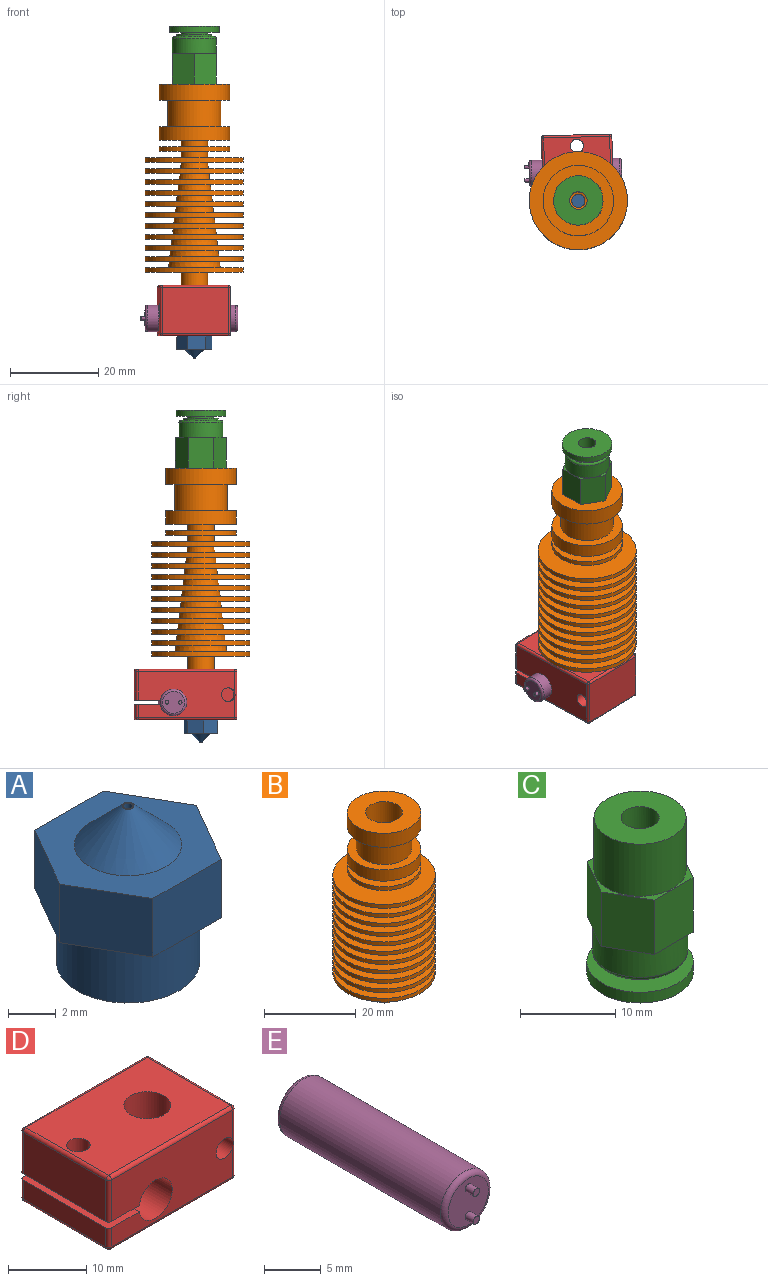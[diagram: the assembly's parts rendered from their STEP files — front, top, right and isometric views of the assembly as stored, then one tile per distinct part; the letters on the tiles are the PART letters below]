
ASSEMBLY  parts=5 mates=7
PART A: 14 faces, bbox 8.1x7x8 mm
  f0: plane 3.5x3mm, normal (0.87,-0.5,0), area 12.1mm2, adj f1,f5,f7,f8
  f1: plane 3.5x3mm, normal (0.87,0.5,0), area 12.1mm2, adj f0,f2,f7,f8
  f2: plane 4.04x3mm, normal (0,1,0), area 12.1mm2, adj f1,f3,f7,f8
  f3: plane 3.5x3mm, normal (-0.87,0.5,0), area 12.1mm2, adj f2,f4,f7,f8
  f4: plane 3.5x3mm, normal (-0.87,-0.5,0), area 12.1mm2, adj f3,f5,f7,f8
  f5: plane 4.04x3mm, normal (0,-1,0), area 12.1mm2, adj f0,f4,f7,f8
  f6: cylinder r=0.2mm len=5mm, axis (0,0,-1), area 6.3mm2, adj f9,f13
  f7: plane 8.08x7mm, normal (0,0,1), area 26.5mm2, adj f0,f1,f2,f3,f4,f5,f10
  f8: plane 8.08x7mm, normal (0,0,-1), area 14.2mm2, adj f0,f1,f2,f3,f4,f5,f12
  f9: plane 0.5x0.5mm, normal (0,0,1), area 0.1mm2, adj f6,f10
  f10: cone r=0.25mm half-angle=45deg, axis (0,0,-1), area 22.2mm2, adj f7,f9
  f11: plane 6x6mm, normal (0,0,-1), area 28.3mm2, adj f12
  f12: cylinder r=3mm len=6mm, axis (0,0,1), area 56.5mm2, adj f8,f11
  f13: plane 0.4x0.4mm, normal (0,0,1), area 0.1mm2, adj f6
PART B: 64 faces, bbox 22.3x22.3x48.7 mm
  f0: plane 22.3x22.3mm, normal (0,0,1), area 282mm2, adj f1,f63
  f1: cone r=5.7mm half-angle=6.8deg, axis (0,0,-1), area 55mm2, adj f0,f2
  f2: plane 22.3x22.3mm, normal (0,0,-1), area 288.5mm2, adj f1,f3
  f3: cylinder r=11.15mm len=22.3mm, axis (0,0,1), area 70.1mm2, adj f2,f4
  f4: plane 22.3x22.3mm, normal (0,0,1), area 292.8mm2, adj f3,f5
  f5: cone r=5.4mm half-angle=6.8deg, axis (0,0,-1), area 52.1mm2, adj f4,f6
  f6: plane 22.3x22.3mm, normal (0,0,-1), area 299mm2, adj f5,f7
  f7: cylinder r=11.15mm len=22.3mm, axis (0,0,1), area 70.1mm2, adj f6,f8
  f8: plane 22.3x22.3mm, normal (0,0,1), area 303mm2, adj f7,f9
  f9: cone r=5.1mm half-angle=6.8deg, axis (0,0,-1), area 49.3mm2, adj f8,f10
  f10: plane 22.3x22.3mm, normal (0,0,-1), area 308.9mm2, adj f9,f11
  f11: cylinder r=11.15mm len=22.3mm, axis (0,0,1), area 70.1mm2, adj f10,f12
  f12: plane 22.3x22.3mm, normal (0,0,1), area 312.7mm2, adj f11,f13
  f13: cone r=4.8mm half-angle=6.8deg, axis (0,0,-1), area 46.4mm2, adj f12,f14
  f14: plane 22.3x22.3mm, normal (0,0,-1), area 318.2mm2, adj f13,f15
  f15: cylinder r=11.15mm len=22.3mm, axis (0,0,1), area 70.1mm2, adj f14,f16
  f16: plane 22.3x22.3mm, normal (0,0,1), area 321.8mm2, adj f15,f17
  f17: cone r=4.5mm half-angle=6.8deg, axis (0,0,-1), area 43.6mm2, adj f16,f18
  f18: plane 22.3x22.3mm, normal (0,0,-1), area 327mm2, adj f17,f19
  f19: cylinder r=11.15mm len=22.3mm, axis (0,0,1), area 70.1mm2, adj f18,f20
  f20: plane 22.3x22.3mm, normal (0,0,1), area 330.3mm2, adj f19,f21
  f21: cone r=4.2mm half-angle=6.8deg, axis (0,0,-1), area 40.7mm2, adj f20,f22
  f22: plane 22.3x22.3mm, normal (0,0,-1), area 335.2mm2, adj f21,f23
  f23: cylinder r=11.15mm len=22.3mm, axis (0,0,1), area 70.1mm2, adj f22,f24
  f24: plane 22.3x22.3mm, normal (0,0,1), area 338.3mm2, adj f23,f25
  f25: cone r=3.9mm half-angle=6.8deg, axis (0,0,-1), area 37.9mm2, adj f24,f26
  f26: plane 22.3x22.3mm, normal (0,0,-1), area 342.8mm2, adj f25,f27
  f27: cylinder r=11.15mm len=22.3mm, axis (0,0,1), area 70.1mm2, adj f26,f28
  f28: plane 22.3x22.3mm, normal (0,0,1), area 345.7mm2, adj f27,f29
  f29: cone r=3.6mm half-angle=6.8deg, axis (0,0,-1), area 35mm2, adj f28,f30
  f30: plane 22.3x22.3mm, normal (0,0,-1), area 349.9mm2, adj f29,f31
  f31: cylinder r=11.15mm len=22.3mm, axis (0,0,1), area 70.1mm2, adj f30,f32
  f32: plane 22.3x22.3mm, normal (0,0,1), area 352.5mm2, adj f31,f33
  f33: cone r=3.3mm half-angle=6.8deg, axis (0,0,-1), area 32.2mm2, adj f32,f34
  f34: plane 22.3x22.3mm, normal (0,0,-1), area 356.4mm2, adj f33,f35
  f35: cylinder r=11.15mm len=22.3mm, axis (0,0,1), area 70.1mm2, adj f34,f36
  f36: plane 22.3x22.3mm, normal (0,0,1), area 358.8mm2, adj f35,f37
  f37: cone r=3mm half-angle=6.8deg, axis (0,0,-1), area 29.3mm2, adj f36,f38
  f38: plane 22.3x22.3mm, normal (0,0,-1), area 362.3mm2, adj f37,f39
  f39: cylinder r=11.15mm len=22.3mm, axis (0,0,1), area 70.1mm2, adj f38,f40
  f40: plane 22.3x22.3mm, normal (0,0,1), area 362.3mm2, adj f39,f41
  f41: cylinder r=3mm len=6mm, axis (0,0,1), area 28.3mm2, adj f40,f42
  f42: plane 16x16mm, normal (0,0,-1), area 172.8mm2, adj f41,f43
  f43: cylinder r=8mm len=16mm, axis (0,0,1), area 50.3mm2, adj f42,f44
  f44: plane 16x16mm, normal (0,0,1), area 172.8mm2, adj f43,f45
  f45: cylinder r=3mm len=6mm, axis (0,0,1), area 28.3mm2, adj f44,f46
  f46: plane 16x16mm, normal (0,0,-1), area 172.8mm2, adj f45,f47
  f47: cylinder r=8mm len=16mm, axis (0,0,1), area 150.8mm2, adj f46,f48
  f48: plane 16x16mm, normal (0,0,1), area 88mm2, adj f47,f49
  f49: cylinder r=6mm len=12mm, axis (0,0,1), area 226.2mm2, adj f48,f50
  f50: plane 16x16mm, normal (0,0,-1), area 88mm2, adj f49,f51
  f51: cylinder r=8mm len=16mm, axis (0,0,1), area 186mm2, adj f50,f52
  f52: plane 16x16mm, normal (0,0,1), area 150.8mm2, adj f51,f53
  f53: cylinder r=4mm len=8mm, axis (0,0,1), area 165.7mm2, adj f52,f54
  f54: cone r=4mm half-angle=46.2deg, axis (0,0,1), area 52.2mm2, adj f53,f55
  f55: cylinder r=2mm len=24.95mm, axis (0,0,1), area 313.5mm2, adj f54,f56
  f56: plane 7x7mm, normal (0,0,-1), area 25.9mm2, adj f55,f57
  f57: cylinder r=3.5mm len=8.24mm, axis (0,0,1), area 181.2mm2, adj f56,f58
  f58: cone r=1.5mm half-angle=74.1deg, axis (0,0,1), area 32.7mm2, adj f57,f59
  f59: cylinder r=1.5mm len=6.43mm, axis (0,0,1), area 60.6mm2, adj f58,f60
  f60: plane 6x6mm, normal (0,0,-1), area 21.2mm2, adj f59,f61
  f61: cylinder r=3mm len=6mm, axis (0,0,1), area 113.1mm2, adj f60,f62
  f62: plane 22.3x22.3mm, normal (0,0,-1), area 362.3mm2, adj f61,f63
  f63: cylinder r=11.15mm len=22.3mm, axis (0,0,1), area 70.1mm2, adj f0,f62
PART C: 25 faces, bbox 11.5x11.2x19.9 mm
  f0: cylinder r=5.61mm len=11.22mm, axis (0,0,-1), area 48.3mm2, adj f1,f2
  f1: plane 11.22x11.22mm, normal (0,0,1), area 70.6mm2, adj f0,f3
  f2: plane 11.22x11.22mm, normal (0,0,-1), area 86.3mm2, adj f0,f24
  f3: cylinder r=3mm len=6mm, axis (0,0,-1), area 9.4mm2, adj f1,f5
  f4: cylinder r=4mm len=8mm, axis (0,0,-1), area 12.6mm2, adj f5,f7
  f5: plane 8x8mm, normal (0,0,-1), area 22mm2, adj f3,f4
  f6: cylinder r=5mm len=10mm, axis (0,0,-1), area 105.2mm2, adj f8,f9,f10,f11,f12,f13,f14
  f7: plane 9x9mm, normal (0,0,-1), area 13.4mm2, adj f4,f8
  f8: torus R=4.5mm, axis (0,0,1), area 23.8mm2, adj f6,f7
  f9: plane 4.33x2.5mm, normal (0,0,-1), area 1.3mm2, adj f6,f17,f18
  f10: plane 4.33x2.5mm, normal (0,0,-1), area 1.3mm2, adj f6,f18,f19
  f11: plane 5x1.44mm, normal (0,0,-1), area 1.3mm2, adj f6,f19,f20
  f12: plane 4.33x2.5mm, normal (0,0,-1), area 1.3mm2, adj f6,f15,f20
  f13: plane 4.33x2.5mm, normal (0,0,-1), area 1.3mm2, adj f6,f15,f16
  f14: plane 5x1.44mm, normal (0,0,-1), area 1.3mm2, adj f6,f16,f17
  f15: plane 7x5.77mm, normal (0,-1,0), area 40.4mm2, adj f12,f13,f16,f20,f21
  f16: plane 7x5mm, normal (0.87,-0.5,0), area 40.4mm2, adj f13,f14,f15,f17,f21
  f17: plane 7x5mm, normal (0.87,0.5,0), area 40.4mm2, adj f9,f14,f16,f18,f21
  f18: plane 7x5.77mm, normal (0,1,0), area 40.4mm2, adj f9,f10,f17,f19,f21
  f19: plane 7x5mm, normal (-0.87,0.5,0), area 40.4mm2, adj f10,f11,f18,f20,f21
  f20: plane 7x5mm, normal (-0.87,-0.5,0), area 40.4mm2, adj f11,f12,f15,f19,f21
  f21: plane 11.55x10mm, normal (0,0,1), area 12.7mm2, adj f15,f16,f17,f18,f19,f20,f22
  f22: cylinder r=4.85mm len=9.7mm, axis (0,0,-1), area 204.2mm2, adj f21,f23
  f23: plane 9.7x9.7mm, normal (0,0,1), area 61.3mm2, adj f22,f24
  f24: cylinder r=2mm len=19.92mm, axis (0,0,-1), area 250.3mm2, adj f2,f23
PART D: 37 faces, bbox 23x16x11.5 mm
  f0: plane 22x15mm, normal (0,0,-1), area 294.7mm2, adj f12,f14,f25,f30,f33,f36
  f1: plane 15x10.5mm, normal (1,0,0), area 157.5mm2, adj f22,f31,f32,f36
  f2: plane 22x15mm, normal (0,0,1), area 294.7mm2, adj f13,f14,f16,f21,f22,f23
  f3: plane 15x6.5mm, normal (-1,0,0), area 97.5mm2, adj f4,f15,f16,f17
  f4: plane 16x5.54mm, normal (0,0,-1), area 81.5mm2, adj f3,f5,f8,f9,f13,f15,f17
  f5: cylinder r=3mm len=16mm, axis (0,1,0), area 285.5mm2, adj f4,f6,f8,f9
  f6: plane 16x5.54mm, normal (0,0,1), area 81.5mm2, adj f5,f7,f8,f9,f12,f20,f24
  f7: plane 15x3mm, normal (-1,0,0), area 45mm2, adj f6,f20,f24,f25
  f8: plane 22x10.5mm, normal (0,-1,0), area 190.2mm2, adj f4,f5,f6,f10,f15,f20,f21,f30
  f9: plane 22x10.5mm, normal (0,1,0), area 197.7mm2, adj f4,f5,f6,f17,f23,f24,f32,f33
  f10: cylinder r=1.55mm len=10mm, axis (0,-1,0), area 97.4mm2, adj f8,f11,f31
  f11: plane 3.1x3.1mm, normal (0,-1,0), area 7.5mm2, adj f10
  f12: cylinder r=1.5mm len=3.5mm, axis (0,0,1), area 33mm2, adj f0,f6
  f13: cylinder r=1.5mm len=7mm, axis (0,0,1), area 66mm2, adj f2,f4
  f14: cylinder r=3mm len=11.5mm, axis (0,0,1), area 216.8mm2, adj f0,f2
  f15: cylinder r=0.5mm len=6.5mm, axis (0,0,1), area 5.1mm2, adj f3,f4,f8,f18
  f16: cylinder r=0.5mm len=15mm, axis (0,-1,0), area 11.8mm2, adj f2,f3,f18,f19
  f17: cylinder r=0.5mm len=6.5mm, axis (0,0,-1), area 5.1mm2, adj f3,f4,f9,f19
  f18: sphere r=0.5mm, area 0.4mm2, adj f15,f16,f21
  f19: sphere r=0.5mm, area 0.4mm2, adj f16,f17,f23
  f20: cylinder r=0.5mm len=3mm, axis (0,0,1), area 2.4mm2, adj f6,f7,f8,f26
  f21: cylinder r=0.5mm len=22mm, axis (1,0,0), area 17.3mm2, adj f2,f8,f18,f27
  f22: cylinder r=0.5mm len=15mm, axis (0,1,0), area 11.8mm2, adj f1,f2,f27,f28
  f23: cylinder r=0.5mm len=22mm, axis (-1,0,0), area 17.3mm2, adj f2,f9,f19,f28
  f24: cylinder r=0.5mm len=3mm, axis (0,0,-1), area 2.4mm2, adj f6,f7,f9,f29
  f25: cylinder r=0.5mm len=15mm, axis (0,1,0), area 11.8mm2, adj f0,f7,f26,f29
  f26: sphere r=0.5mm, area 0.4mm2, adj f20,f25,f30
  f27: sphere r=0.5mm, area 0.4mm2, adj f21,f22,f31
  f28: sphere r=0.5mm, area 0.4mm2, adj f22,f23,f32
  f29: sphere r=0.5mm, area 0.4mm2, adj f24,f25,f33
  f30: cylinder r=0.5mm len=22mm, axis (-1,0,0), area 17.3mm2, adj f0,f8,f26,f34
  f31: cylinder r=0.5mm len=10.5mm, axis (0,0,-1), area 8.2mm2, adj f1,f8,f10,f27,f34
  f32: cylinder r=0.5mm len=10.5mm, axis (0,0,1), area 8.2mm2, adj f1,f9,f28,f35
  f33: cylinder r=0.5mm len=22mm, axis (1,0,0), area 17.3mm2, adj f0,f9,f29,f35
  f34: sphere r=0.5mm, area 0.4mm2, adj f30,f31,f36
  f35: sphere r=0.5mm, area 0.4mm2, adj f32,f33,f36
  f36: cylinder r=0.5mm len=15mm, axis (0,-1,0), area 11.8mm2, adj f0,f1,f34,f35
PART E: 9 faces, bbox 6.5x22x6.5 mm
  f0: cylinder r=3mm len=20mm, axis (0,1,0), area 377mm2, adj f3,f4
  f1: plane 5x5mm, normal (0,-1,0), area 18.6mm2, adj f4,f5,f7
  f2: plane 5x5mm, normal (0,1,0), area 19.6mm2, adj f3
  f3: torus R=2.5mm, axis (0,-1,0), area 13.9mm2, adj f0,f2
  f4: torus R=2.5mm, axis (0,-1,0), area 13.9mm2, adj f0,f1
  f5: cylinder r=0.4mm len=1mm, axis (0,1,0), area 2.5mm2, adj f1,f6
  f6: plane 0.8x0.8mm, normal (0,-1,0), area 0.5mm2, adj f5
  f7: cylinder r=0.4mm len=1mm, axis (0,1,0), area 2.5mm2, adj f1,f8
  f8: plane 0.8x0.8mm, normal (0,-1,0), area 0.5mm2, adj f7
PLACE A rot(axis=(0.43,0.9,0),180deg) t=(-6.41,22.84,-22.76)mm
PLACE B t=(-6.41,22.84,-8.26)mm fixed
PLACE C rot(axis=(0.71,0.71,0),180deg) t=(-6.41,22.84,47.66)mm
PLACE D rot(axis=(0,0,-1),88.5deg) t=(-6.5,26.34,-17.01)mm
PLACE E rot(axis=(0.57,0.59,-0.57),119.1deg) t=(-7.08,29.33,-18.76)mm
MATE planar D.f9 <-> E.f0  axis (1,0.03,0) through (1.52,25.91,-16.72)mm
MATE planar A.f8 <-> D.f0  axis (0,0,1) through (-3.86,19.7,-22.76)mm
MATE cylindrical D.f14 <-> A.f12  axis (0,0,1) through (-6.41,22.84,-17.01)mm
MATE planar C.f21 <-> B.f1  axis (0,0,-1) through (-8.91,27.17,34.44)mm
MATE cylindrical D.f5 <-> E.f0  axis (1,0.03,0) through (1.42,29.55,-18.76)mm
MATE cylindrical D.f14 <-> B.f1  axis (0,0,1) through (-6.41,22.84,-17.01)mm
MATE planar D.f2 <-> B.f1  axis (0,0,1) through (-6.5,26.46,-11.26)mm
